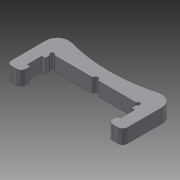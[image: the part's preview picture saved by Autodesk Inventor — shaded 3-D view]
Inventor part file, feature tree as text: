
AUTODESK INVENTOR PART (.ipt)
format: ipt  version: 2015 (Build 190159000, 159)  size: 147,968 bytes
history: native  units: mm
features: fillet x4, extrude x2, sketch x2
ambient origin geometry x8: Origin, YZ Plane, XZ Plane, XY Plane, X Axis, Y Axis, Z Axis, Center Point
bodies: Solid1 (feature_tree)
feature tree (8):
  extrude  "Extrusion1"  Depth=6.2mm
  fillet  "Fillet1"  Radius=1.5mm
  fillet  "Fillet2"  Radius=4.0mm
  fillet  "Fillet3"  Radius=5.0mm
  extrude  "Extrusion2"  Depth=5.0mm
  fillet  "Fillet4"  Radius=0.8mm
  sketch  "Sketch1"  dims[d0=6.0mm d4=6.2mm d5=1.5mm d7=4.0mm d9=5.0mm]
  sketch  "Sketch2"  dims[d10=70.0mm d11=5.0mm d12=0.8mm d13=3.0mm d14=6.0mm d15=0.0mm d16=2.0mm d17=0.5mm d18=1.4mm d19=0.5mm d20=18.5mm d21=0.25mm d22=10.0mm d23=0.0mm d24=0.5mm d25=1.0mm d26=8.715839mm]
